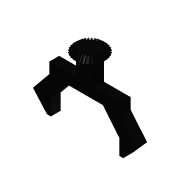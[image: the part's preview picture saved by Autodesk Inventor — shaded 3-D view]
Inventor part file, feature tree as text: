
AUTODESK INVENTOR PART (.ipt)
format: ipt  version: 2016 (Build 200138000, 138)  size: 576,512 bytes
history: native  units: mm
features: other x16, sketch x3, extrude x2, mirror x1, projected_geometry x1
ambient origin geometry x6: Origin, XZ Plane, X Axis, Y Axis, Z Axis, Center Point
bodies: Solid1 (feature_tree)
feature tree (23):
  other  "Top Point"
  other  "Mesh Plane2"
  other  "Teeth Body"
  other  "Start Point"
  other  "Tooth Plane"
  other  "Start Sketch"
  other  "End Point"
  other  "Fix Body"
  extrude  "Extrusion1"  Depth=45.276163mm
  mirror  "Mirror1"
  extrude  "Extrusion2"  Depth=9.525mm
  other  "Mesh Plane"
  other  "Top Plane"
  other  "Teeth Body Sketch"
  other  "End Plane"
  other  "End Sketch"
  other  "Body Sketch"
  sketch  "Sketch6"  dims[d0=47.811765mm d1=45.276163mm]
  other  "Srf1"
  sketch  "Sketch8"  dims[d2=49.924766mm d3=9.525mm]
  projected_geometry  "Projected Loop1"
  sketch  "Sketch9"  dims[d4=22.849382mm d5=90.0deg d7=12.077204mm d8=12.386496mm d9=29.30193mm d11=9.689353mm d12=8.627964mm d15=8.848923mm d16=20.933322mm d17=0.0mm d18=90.0deg d19=0.0mm d20=90.0deg d21=320.0mm d22=360.0deg d46=90.0deg d47=90.0deg d48=0.0mm d49=0.0mm d50=90.0deg d51=0.981748mm d52=0.0mm d53=0.0mm d54=0.0mm d57=36.288258mm d58=31.620635mm d59=25.92436mm d60=22.589806mm d88=0.0mm d89=0.0mm d90=14.2875mm d91=53.975mm d92=17.4625mm d93=22.225mm d94=41.275mm d95=6.35mm d96=25.4mm d97=28.575mm d98=15.875mm d99=0.0mm d100=6.35mm d101=2.54mm d102=0.0mm]
  other  "Pitch Diameter"
